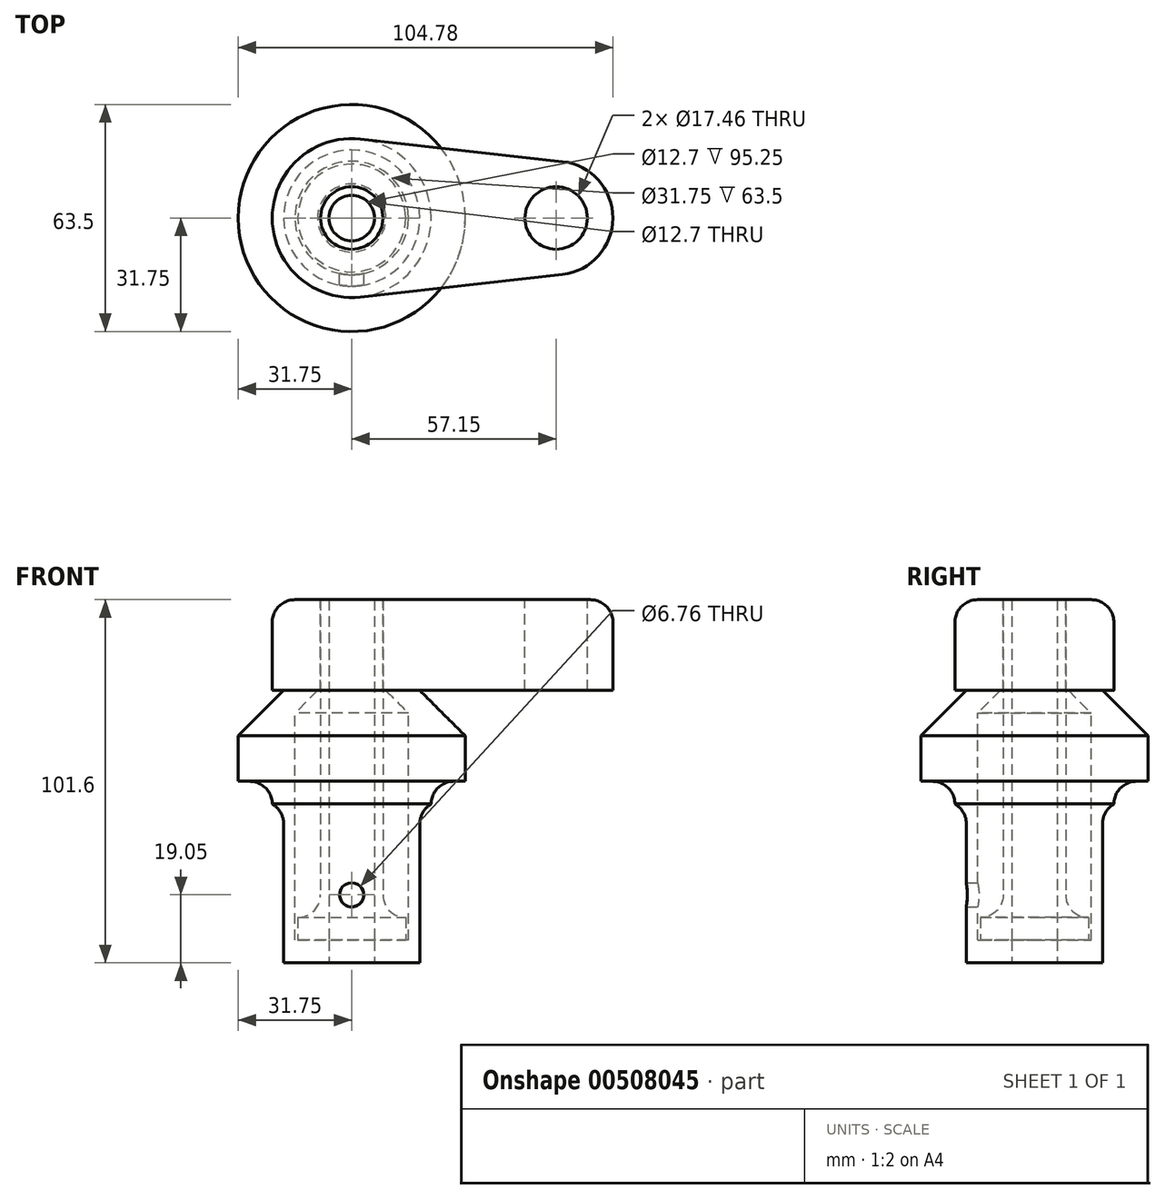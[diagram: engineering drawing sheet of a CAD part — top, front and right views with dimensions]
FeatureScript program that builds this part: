
annotation { "Feature Type Name" : "Feature", "Feature Type Description" : "" }
export const myFeature = defineFeature(function(context is Context, id is Id, definition is map)
    precondition{}
    {
        {
            var Q0;
            Q0=qCreatedBy(makeId("Front.planeOp"),FACE);
            var sketch = newSketch(context, id + "F0", { "sketchPlane" : qUnion([Q0])});
            skLineSegment(sketch, "E0", {"start": v(0, 0) * mm, "end": v(0, 76.2) * mm});
            skLineSegment(sketch, "E1", {"start": v(0, 76.2) * mm, "end": v(19.05, 76.2) * mm});
            skLineSegment(sketch, "E2", {"start": v(19.05, 76.2) * mm, "end": v(31.75, 63.5) * mm});
            skLineSegment(sketch, "E3", {"start": v(31.75, 63.5) * mm, "end": v(31.75, 50.8) * mm});
            skLineSegment(sketch, "E4", {"start": v(31.75, 50.8) * mm, "end": v(22.23, 50.8) * mm});
            skLineSegment(sketch, "E5", {"start": v(22.23, 50.8) * mm, "end": v(22.23, 44.45) * mm});
            skLineSegment(sketch, "E6", {"start": v(22.23, 44.45) * mm, "end": v(19.05, 44.45) * mm});
            skLineSegment(sketch, "E7", {"start": v(19.05, 44.45) * mm, "end": v(19.05, 0) * mm});
            skLineSegment(sketch, "E8", {"start": v(19.05, 0) * mm, "end": v(0, 0) * mm});
            skLineSegment(sketch, "E9", {"start": v(9.53, 76.2) * mm, "end": v(15.88, 69.85) * mm});
            skLineSegment(sketch, "E10", {"start": v(15.88, 69.85) * mm, "end": v(15.88, 6.35) * mm});
            skLineSegment(sketch, "E11", {"start": v(15.88, 6.35) * mm, "end": v(0, 6.35) * mm});
            skLineSegment(sketch, "E12", {"start": v(0, 76.2) * mm, "end": v(0, 91.26) * mm, "construction": true});
            skLineSegment(sketch, "E13", {"start": v(0, 76.2) * mm, "end": v(0, 101.6) * mm});
            skLineSegment(sketch, "E14", {"start": v(0, 101.6) * mm, "end": v(8.73, 101.6) * mm});
            skLineSegment(sketch, "E15", {"start": v(8.73, 101.6) * mm, "end": v(8.73, 12.7) * mm});
            skLineSegment(sketch, "E16", {"start": v(8.73, 12.7) * mm, "end": v(15.08, 12.7) * mm});
            skLineSegment(sketch, "E17", {"start": v(15.08, 12.7) * mm, "end": v(15.08, 6.35) * mm});
            skSolve(sketch);
        }
        {
            var Q0;
            {var subQ5=sQuery(id+"F0.wireOp",EDGE,"E2");Q0=makeQuery(id+"F0.imprint","IMPRINT",FACE,{"disambiguationData":[TD([[makeQuery(id+"F0.imprint","IMPRINT",EDGE,{"derivedFrom":subQ5}),-1.0]])]});}
            var Q1;
            Q1=sQuery(id+"F0.wireOp",EDGE,"E0");
            revolve(context, id + "F1", {"entities" : qUnion([Q0]), "axis" : qUnion([Q1]), "revolveType" : RevolveType.FULL, "oppositeDirection" : true});
        }
        {
            var Q0;
            {var subQ0=sQuery(id+"F0.wireOp",EDGE,"E13");Q0=makeQuery(id+"F0.imprint","IMPRINT",FACE,{"disambiguationData":[TD([[makeQuery(id+"F0.imprint","IMPRINT",EDGE,{"derivedFrom":subQ0}),-1.0]])]});}
            var Q1;
            {var subQ0=sQuery(id+"F0.wireOp",EDGE,"E16");Q1=makeQuery(id+"F0.imprint","IMPRINT",FACE,{"disambiguationData":[TD([[makeQuery(id+"F0.imprint","IMPRINT",EDGE,{"derivedFrom":subQ0}),-1.0]])]});}
            var Q2;
            Q2=sQuery(id+"F0.wireOp",EDGE,"E0");
            revolve(context, id + "F2", {"entities" : qUnion([Q0, Q1]), "axis" : qUnion([Q2]), "revolveType" : RevolveType.FULL});
        }
        {
            var Q0;
            Q0=makeQuery(id+"F2.opRevolve","SWEPT_FACE",FACE,{"disambiguationData":[OSD([sQuery(id+"F0.wireOp",EDGE,"E14")])]});
            var sketch = newSketch(context, id + "F3", { "sketchPlane" : qUnion([Q0])});
            skCircle(sketch, "E18", {"center": v(0, 0) * mm, "radius": 22.23 * mm});
            skCircle(sketch, "E19", {"center": v(57.15, 0) * mm, "radius": 15.88 * mm});
            skLineSegment(sketch, "E20", {"start": v(58.91, 15.78) * mm, "end": v(2.47, 22.09) * mm});
            skLineSegment(sketch, "E21", {"start": v(58.91, -15.78) * mm, "end": v(2.47, -22.09) * mm});
            skCircle(sketch, "E22.0", {"center": v(0, 0) * mm, "radius": 8.73 * mm});
            skCircle(sketch, "E23", {"center": v(57.15, 0) * mm, "radius": 8.73 * mm});
            skSolve(sketch);
        }
        {
            var Q0;
            Q0 = qSketchRegion(id + "F3", true);
            var Q1;
            Q1=makeQuery(id+"F1.opRevolve","SWEPT_FACE",FACE,{"disambiguationData":[OSD([sQuery(id+"F0.wireOp",EDGE,"E1")])]});
            extrude(context, id + "F4", {"entities" : qUnion([Q0]), "oppositeDirection" : true, "endBoundEntityFace" : qUnion([Q1]), "depth" : 25.4 * mm});
        }
        {
            var Q0;
            Q0=qCreatedBy(makeId("Front.planeOp"),FACE);
            var sketch = newSketch(context, id + "F5", { "sketchPlane" : qUnion([Q0])});
            skPoint(sketch, "E24", {"position": v(0, 19.05) * mm});
            skSolve(sketch);
        }
        {
            var Q0;
            Q0=sQuery(id+"F5.wireOp",VERTEX,"E24");
            var Q1;
            Q1=makeQuery(id+"F1.opRevolve","SWEPT_BODY",BODY,{"disambiguationData":[OSD([sQuery(id+"F0.wireOp",EDGE,"E0"),sQuery(id+"F0.wireOp",EDGE,"E1"),sQuery(id+"F0.wireOp",EDGE,"E2"),sQuery(id+"F0.wireOp",EDGE,"E3"),sQuery(id+"F0.wireOp",EDGE,"E4"),sQuery(id+"F0.wireOp",EDGE,"E5"),sQuery(id+"F0.wireOp",EDGE,"E6"),sQuery(id+"F0.wireOp",EDGE,"E7"),sQuery(id+"F0.wireOp",EDGE,"E8"),sQuery(id+"F0.wireOp",EDGE,"E9"),sQuery(id+"F0.wireOp",EDGE,"E10"),sQuery(id+"F0.wireOp",EDGE,"E11")])]});
            hole(context, id + "F6", {"style" : HoleStyle.SIMPLE, "endStyle" : HoleEndStyle.THROUGH, "oppositeDirection" : true, "standardTappedOrClearance" : lookupTablePath({ "standard" : "ANSI", "fit" : "Normal (ASME)", "size" : "1/4", "type" : "Clearance" }), "standardBlindInLast" : lookupTablePath({ "fit" : "Free", "standard" : "ANSI", "size" : "1/4", "type" : "Clearance" }), "holeDiameter" : 6.76 * mm, "tappedDepth" : 14.3 * mm, "tapClearance" : 3, "locations" : qUnion([Q0]), "scope" : qUnion([Q1])});
        }
        {
            var Q0;
            Q0=makeQuery(id+"F4.opExtrude","CAP_EDGE",EDGE,{"disambiguationData":[OSD([sQuery(id+"F3.wireOp",EDGE,"E20")])],"isStart":true});
            var Q1;
            Q1=makeQuery(id+"F2.opRevolve","SWEPT_EDGE",EDGE,{"disambiguationData":[OSD([sQuery(id+"F0.wireOp",EDGE,"E15"),sQuery(id+"F0.wireOp",EDGE,"E16")])]});
            var Q2;
            Q2=makeQuery(id+"F1.opRevolve","SWEPT_EDGE",EDGE,{"disambiguationData":[OSD([sQuery(id+"F0.wireOp",EDGE,"E4"),sQuery(id+"F0.wireOp",EDGE,"E5")])]});
            var Q3;
            Q3=makeQuery(id+"F1.opRevolve","SWEPT_EDGE",EDGE,{"disambiguationData":[OSD([sQuery(id+"F0.wireOp",EDGE,"E6"),sQuery(id+"F0.wireOp",EDGE,"E7")])]});
            fillet(context, id + "F7", {"entities" : qUnion([Q0, Q1, Q2, Q3]), "radius" : 6.35 * mm, "tangentPropagation" : true, "allowEdgeOverflow" : false});
        }
        {
            var Q0;
            Q0=makeQuery(id+"F1.opRevolve","SWEPT_FACE",FACE,{"disambiguationData":[OSD([sQuery(id+"F0.wireOp",EDGE,"E8")])]});
            var sketch = newSketch(context, id + "F8", { "sketchPlane" : qUnion([Q0])});
            skCircle(sketch, "E25", {"center": v(0, 0) * mm, "radius": 6.35 * mm});
            skSolve(sketch);
        }
        {
            var Q0;
            Q0 = qSketchRegion(id + "F8", true);
            extrude(context, id + "F9", {"entities" : qUnion([Q0]), "operationType" : NewBodyOperationType.REMOVE, "endBound" : BoundingType.THROUGH_ALL, "oppositeDirection" : true, "depth" : 25.4 * mm});
        }
    });
